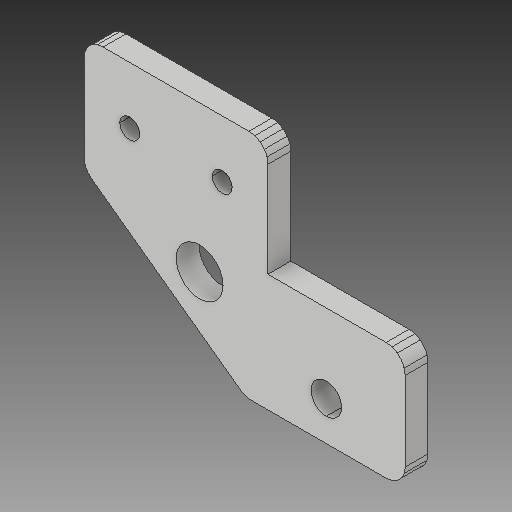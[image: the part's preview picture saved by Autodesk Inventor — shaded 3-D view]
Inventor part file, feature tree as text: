
AUTODESK INVENTOR PART (.ipt)
format: ipt  version: 2018 (Build 220112000, 112)  size: 243,712 bytes
history: native  units: mm
features: other x3, sketch x3, extrude x1
ambient origin geometry x8: Origin, YZ Plane, XZ Plane, XY Plane, X Axis, Y Axis, Z Axis, Center Point
bodies: Solid1 (feature_tree)
feature tree (7):
  other  "Leadscrew-rod-holder.ipt"
  extrude  "Extrusion1"  Depth=10.0mm TaperAngle=0.0deg
  other  "Solid1::Leadscrew-rod-holder.ipt"
  other  "TaggingFeature1"
  sketch  "Sketch1"  dims[d0=10.0mm d1=10.0mm d2=0.0mm]
  sketch  "Sketch2"  dims[d3=12.3mm]
  sketch  "Sketch3"
